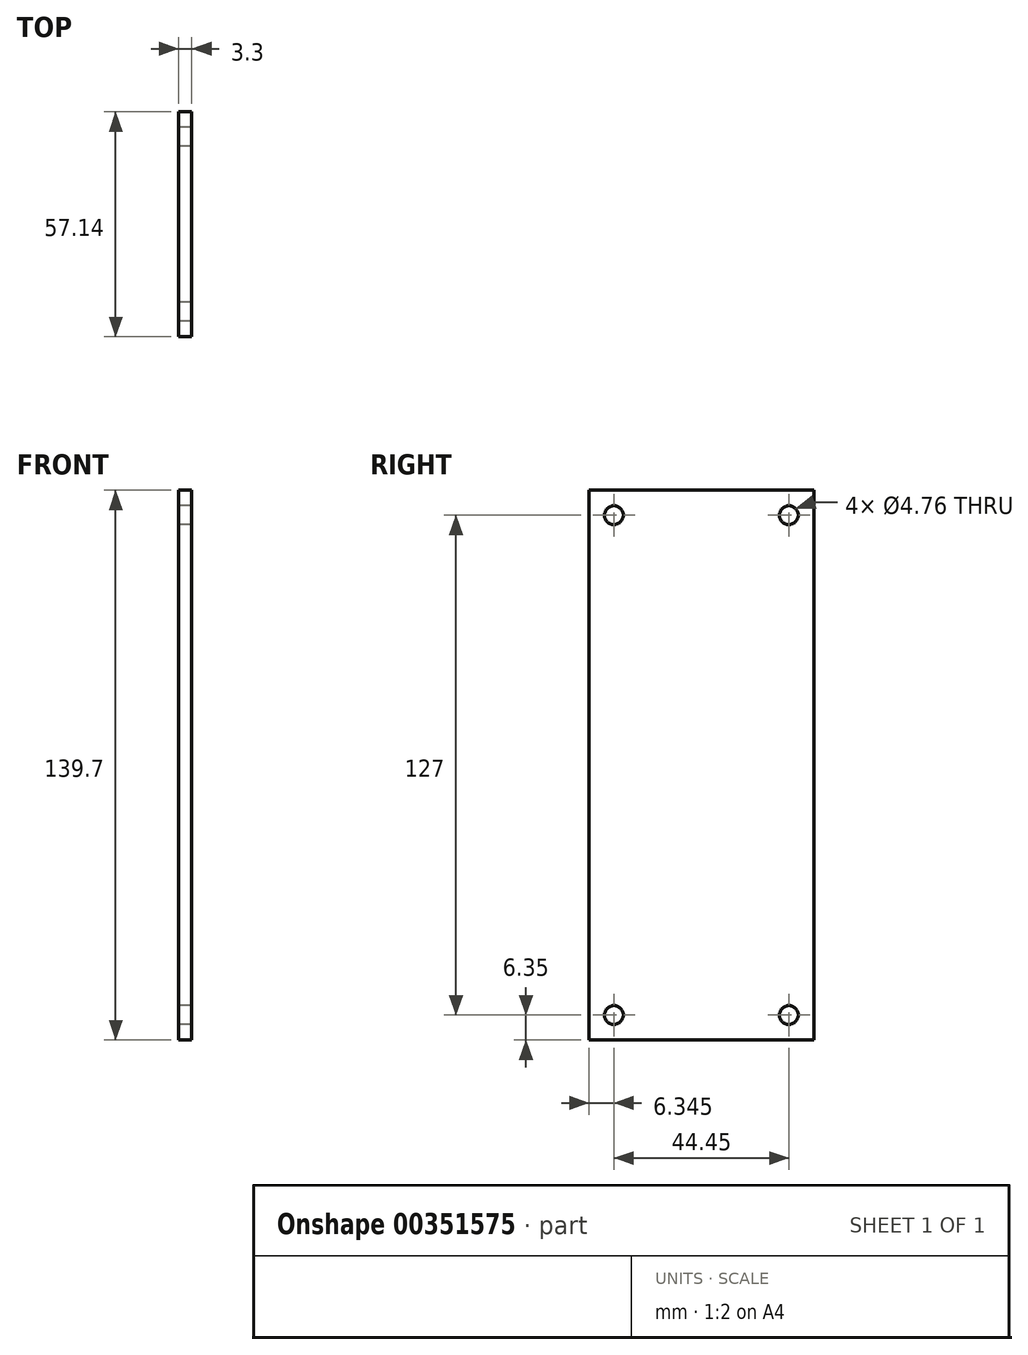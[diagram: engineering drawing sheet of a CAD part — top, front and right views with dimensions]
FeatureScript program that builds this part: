
annotation { "Feature Type Name" : "Feature", "Feature Type Description" : "" }
export const myFeature = defineFeature(function(context is Context, id is Id, definition is map)
    precondition{}
    {
        {
            var Q0;
            Q0=qCreatedBy(makeId("Top.planeOp"),FACE);
            var sketch = newSketch(context, id + "F0", { "sketchPlane" : qUnion([Q0])});
            skLineSegment(sketch, "E0.bottom", {"start": v(1.65, -28.58) * mm, "end": v(-1.65, -28.58) * mm});
            skLineSegment(sketch, "E0.top", {"start": v(1.65, 28.58) * mm, "end": v(-1.65, 28.58) * mm});
            skLineSegment(sketch, "E0.left", {"start": v(1.65, -28.58) * mm, "end": v(1.65, 28.58) * mm});
            skLineSegment(sketch, "E0.right", {"start": v(-1.65, -28.58) * mm, "end": v(-1.65, 28.58) * mm});
            skPoint(sketch, "E0.middle", {"position": v(0, 0) * mm});
            skSolve(sketch);
        }
        {
            var Q0;
            Q0 = qSketchRegion(id + "F0", true);
            extrude(context, id + "F1", {"entities" : qUnion([Q0]), "depth" : 139.7 * mm, "symmetric" : true});
        }
        {
            var Q0;
            Q0=makeQuery(id+"F1.opExtrude","SWEPT_FACE",FACE,{"disambiguationData":[OSD([sQuery(id+"F0.wireOp",EDGE,"E0.right")])]});
            var sketch = newSketch(context, id + "F2", { "sketchPlane" : qUnion([Q0])});
            skCircle(sketch, "E1", {"center": v(-22.23, 63.5) * mm, "radius": 2.38 * mm});
            skCircle(sketch, "E2.MirrorC", {"center": v(22.23, 63.5) * mm, "radius": 2.38 * mm});
            skCircle(sketch, "E3.MirrorC", {"center": v(-22.23, -63.5) * mm, "radius": 2.38 * mm});
            skCircle(sketch, "E4.MirrorC", {"center": v(22.23, -63.5) * mm, "radius": 2.38 * mm});
            skSolve(sketch);
        }
        {
            var Q0;
            Q0 = qSketchRegion(id + "F2", true);
            var Q1;
            Q1=makeQuery(id+"F1.opExtrude","SWEPT_FACE",FACE,{"disambiguationData":[OSD([sQuery(id+"F0.wireOp",EDGE,"E0.left")])]});
            extrude(context, id + "F3", {"entities" : qUnion([Q0]), "operationType" : NewBodyOperationType.REMOVE, "endBound" : BoundingType.UP_TO_SURFACE, "oppositeDirection" : true, "endBoundEntityFace" : qUnion([Q1]), "depth" : 25.4 * mm});
        }
    });
